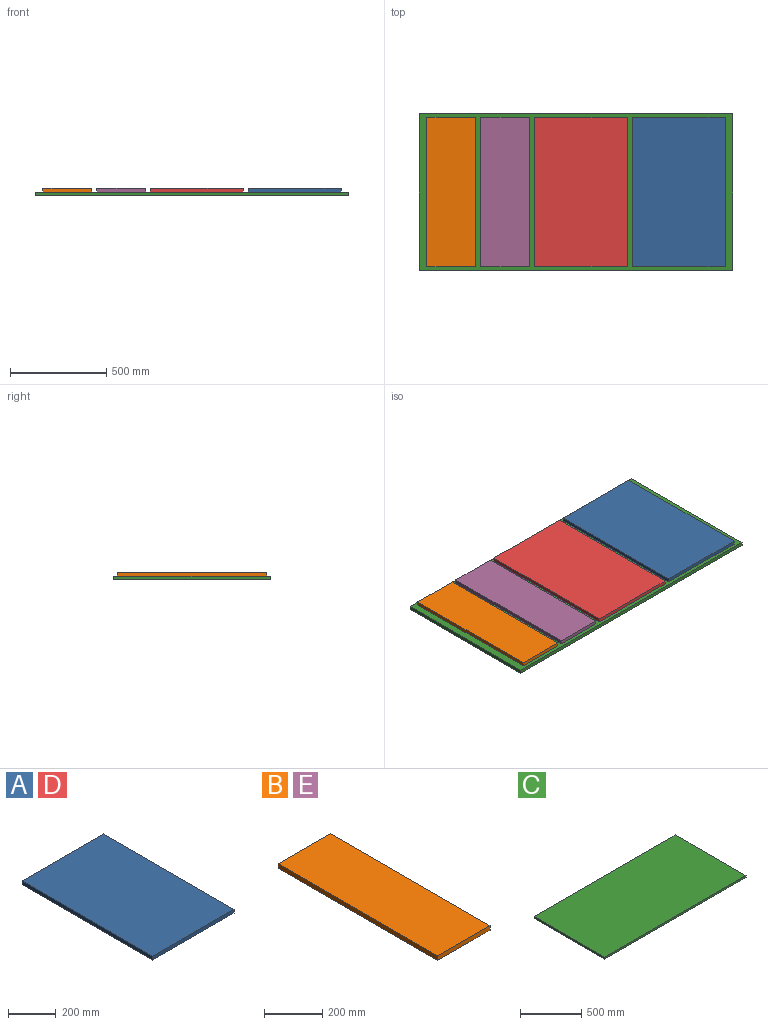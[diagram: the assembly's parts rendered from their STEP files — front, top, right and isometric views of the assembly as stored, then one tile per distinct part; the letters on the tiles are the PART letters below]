
ASSEMBLY  parts=5 mates=4
PART A: 6 faces, bbox 482.6x774.7x19.1 mm
  f0: plane 482.6x19.05mm, normal (0,1,0), area 9193.5mm2, adj f1,f3,f4,f5
  f1: plane 774.7x19.05mm, normal (-1,0,0), area 14758mm2, adj f0,f2,f4,f5
  f2: plane 482.6x19.05mm, normal (0,-1,0), area 9193.5mm2, adj f1,f3,f4,f5
  f3: plane 774.7x19.05mm, normal (1,0,0), area 14758mm2, adj f0,f2,f4,f5
  f4: plane 774.7x482.6mm, normal (0,0,1), area 373870.2mm2, adj f0,f1,f2,f3
  f5: plane 774.7x482.6mm, normal (0,0,-1), area 373870.2mm2, adj f0,f1,f2,f3
PART B: 6 faces, bbox 254x774.7x19.1 mm
  f0: plane 254x19.05mm, normal (0,1,0), area 4838.7mm2, adj f1,f3,f4,f5
  f1: plane 774.7x19.05mm, normal (-1,0,0), area 14758mm2, adj f0,f2,f4,f5
  f2: plane 254x19.05mm, normal (0,-1,0), area 4838.7mm2, adj f1,f3,f4,f5
  f3: plane 774.7x19.05mm, normal (1,0,0), area 14758mm2, adj f0,f2,f4,f5
  f4: plane 774.7x254mm, normal (0,0,1), area 196773.8mm2, adj f0,f1,f2,f3
  f5: plane 774.7x254mm, normal (0,0,-1), area 196773.8mm2, adj f0,f1,f2,f3
PART C: 6 faces, bbox 1625.6x812.8x19.1 mm
  f0: plane 1625.6x19.05mm, normal (0,1,0), area 30967.7mm2, adj f1,f3,f4,f5
  f1: plane 812.8x19.05mm, normal (-1,0,0), area 15483.8mm2, adj f0,f2,f4,f5
  f2: plane 1625.6x19.05mm, normal (0,-1,0), area 30967.7mm2, adj f1,f3,f4,f5
  f3: plane 812.8x19.05mm, normal (1,0,0), area 15483.8mm2, adj f0,f2,f4,f5
  f4: plane 1625.6x812.8mm, normal (0,0,1), area 1321287.7mm2, adj f0,f1,f2,f3
  f5: plane 1625.6x812.8mm, normal (0,0,-1), area 1321287.7mm2, adj f0,f1,f2,f3
PART D: same geometry as A
PART E: same geometry as B
PLACE A t=(463.9,1072.75,-116.18)mm
PLACE B t=(-165.18,1062.57,-116.18)mm
PLACE C t=(-206.37,69.1,-135.23)mm
PLACE D t=(-44.1,1072.75,-116.18)mm
PLACE E t=(114.22,1062.57,-116.18)mm
MATE fastened D.f4 <-> E.f4  axis (0,0,1) through (-173.75,-450.49,-97.13)mm
MATE fastened B.f5 <-> C.f4  axis (0,0,-1) through (-732.55,-450.49,-116.18)mm
MATE fastened A.f4 <-> D.f4  axis (0,0,1) through (334.25,-450.49,-97.13)mm
MATE fastened E.f4 <-> B.f4  axis (0,0,1) through (-453.15,-450.49,-97.13)mm
